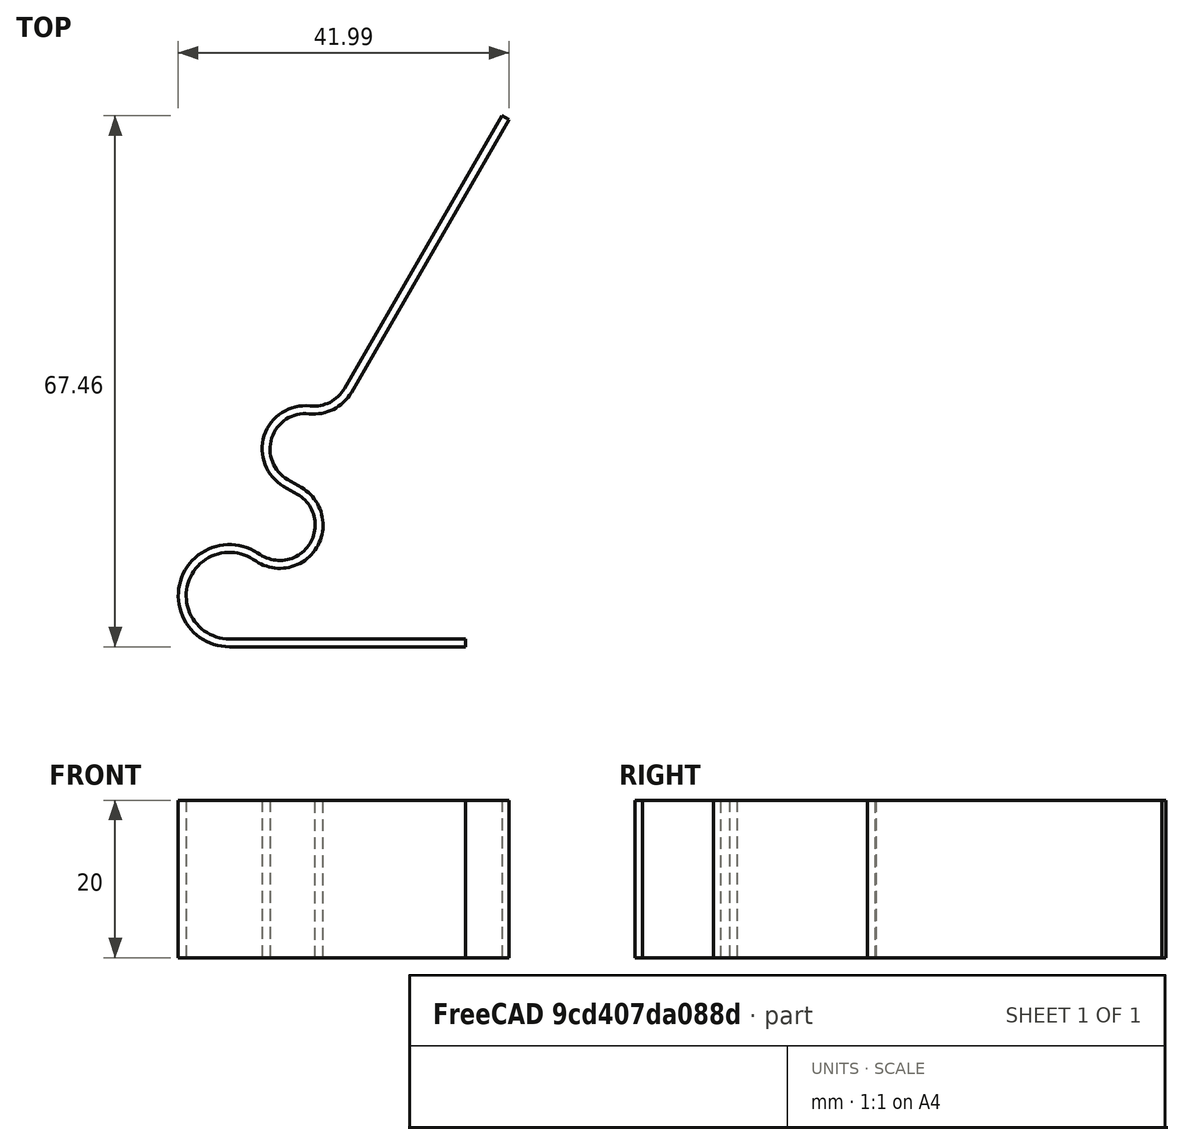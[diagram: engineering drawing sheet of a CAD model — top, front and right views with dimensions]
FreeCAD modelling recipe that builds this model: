
FCSTD DOCUMENT  (FreeCAD 2021.1015R24301 +3962 (Git))
Label: plastic_spring_catapult_1
License: All rights reserved
objects: Sketcher::SketchObject×2, Spreadsheet::Sheet×1, PartDesign::AdditivePipe×1, PartDesign::Body×1
note: 6 computed .brp shape members not serialized (recipe doc carries the construction recipe); baked Part::Feature solids carry a one-line shape summary decoded from their .brp

FEATURE [Spreadsheet::Sheet] Spreadsheet
  PythonMode = false
  cells = A1='height; B1(h)=20; A2='thickness; B2(thk)=1; A3='dia; B3(dia)=10; A4=center length; B4(l_center)=2; A5=center spacing; B5(cs)=10; C5=should be dia/2 really; A6=end length; B6(l_end)=40; A7=base length; B7(base_length)=30; A8=catapult angle; B8(a_catapult)=60; A9=bottom curve diameter; B9(dia_bot)=12
FEATURE [Sketcher::SketchObject] Sketch  label="profile"
  FullyConstrained = true
  MapMode = 5
  Placement = pos=(0,0,0) rot=(0.57735,0.57735,0.57735;2.0944rad)
  Support = -> [YZ_Plane]
  expr: Constraints[10] = Spreadsheet.thk / 2
  expr: Constraints[11] = Spreadsheet.thk
  expr: Constraints[9] = Spreadsheet.h
  sketch-geometry (4):
    g0: LineSegment StartX=-0.5 StartY=0 StartZ=0 EndX=0.5 EndY=0 EndZ=0
    g1: LineSegment StartX=0.5 StartY=0 StartZ=0 EndX=0.5 EndY=20 EndZ=0
    g2: LineSegment StartX=0.5 StartY=20 StartZ=0 EndX=-0.5 EndY=20 EndZ=0
    g3: LineSegment StartX=-0.5 StartY=20 StartZ=0 EndX=-0.5 EndY=0 EndZ=0
  constraints (12):
    c: Coincident(g0,g1)
    c: Coincident(g1,g2)
    c: Coincident(g2,g3)
    c: Coincident(g3,g0)
    c: Horizontal(g0)
    c: Horizontal(g2)
    c: Vertical(g1)
    c: Vertical(g3)
    c: PointOnObject(g0,g-1)
    c: DistanceY(g3,g3) = 20
    c: DistanceX(g0,g-1) = 0.5
    c: DistanceX(g0,g0) = 1
FEATURE [Sketcher::SketchObject] Sketch001  label="path"
  FullyConstrained = false
  MapMode = 5
  Support = -> [XY_Plane]
  expr: Constraints[13] = Spreadsheet.a_catapult
  expr: Constraints[15] = Spreadsheet.dia
  expr: Constraints[16] = Spreadsheet.dia
  expr: Constraints[22] = Spreadsheet.cs
  expr: Constraints[23] = Spreadsheet.dia_bot / 2 + Spreadsheet.dia / 2
  expr: Constraints[24] = Spreadsheet.l_center
  expr: Constraints[25] = Spreadsheet.dia
  expr: Constraints[3] = Spreadsheet.base_length
  expr: Constraints[5] = Spreadsheet.dia_bot
  expr: Constraints[9] = Spreadsheet.l_end
  sketch-geometry (11):
    g0: LineSegment StartX=0 StartY=0 StartZ=0 EndX=-30 EndY=0 EndZ=0
    g1: ArcOfCircle CenterX=-30 CenterY=6 CenterZ=0 NormalX=0 NormalY=0 NormalZ=1 AngleXU=0 Radius=6 StartAngle=0.989803 EndAngle=4.71239
    g2: LineSegment StartX=-26.7069 StartY=11.0155 StartZ=0 EndX=-26.3623 EndY=10.7893 EndZ=0
    g3: ArcOfCircle CenterX=-23.6181 CenterY=14.9689 CenterZ=0 NormalX=0 NormalY=0 NormalZ=1 AngleXU=0 Radius=5 StartAngle=4.1314 EndAngle=7.33038
    g4: LineSegment StartX=-21.1181 StartY=19.299 StartZ=0 EndX=-22.8501 EndY=20.299 EndZ=0
    g5: LineSegment StartX=-14.9476 StartY=32.0715 StartZ=0 EndX=5.05237 EndY=66.7125 EndZ=0
    g6: ArcOfCircle CenterX=-20.3501 CenterY=24.6291 CenterZ=0 NormalX=0 NormalY=0 NormalZ=1 AngleXU=0 Radius=5 StartAngle=1.46335 EndAngle=4.18879
    g7: ArcOfCircle CenterX=-19.2778 CenterY=34.5715 CenterZ=0 NormalX=0 NormalY=0 NormalZ=1 AngleXU=0 Radius=5 StartAngle=4.60495 EndAngle=5.75959
    g8: LineSegment [constr] StartX=-25.3501 StartY=15.9689 StartZ=0 EndX=-23.6181 EndY=14.9689 EndZ=0
    g9: LineSegment [constr] StartX=-25.3501 StartY=15.9689 StartZ=0 EndX=-20.3501 EndY=24.6291 EndZ=0
    g10: LineSegment [constr] StartX=-30 StartY=6 StartZ=0 EndX=5.05237 EndY=66.7125 EndZ=0
  constraints (34):
    c: Coincident(g0,g-1)
    c: PointOnObject(g0,g-1)
    c: Coincident(g1,g0)
    c: DistanceX(g0,g0) = 30
    c: Tangent(g1,g0)
    c: Diameter(g1) = 12
    c: Coincident(g2,g1)
    c: Coincident(g3,g2)
    c: Coincident(g4,g3)
    c: Distance(g5) = 40
    c: Tangent(g4,g3)
    c: Tangent(g2,g3)
    c: Tangent(g1,g2)
    c: Angle(g0,g5) = 1.0472
    c: Tangent(g6,g4)
    c: Diameter(g6) = 10
    c: Diameter(g3) = 10
    c: Coincident(g7,g6)
    c: Coincident(g7,g5)
    c: Tangent(g7,g5)
    c: Tangent(g6,g7)
    c: Coincident(g8,g3)
    c: Distance(g8,g6) = 10
    c: Distance(g1,g8) = 11
    c: Distance(g8) = 2
    c: Diameter(g7) = 10
    c: Coincident(g9,g8)
    c: Coincident(g9,g6)
    c: Coincident(g10,g1)
    c: Parallel(g10,g5)
    c: Coincident(g6,g4)
    c: Perpendicular(g8,g9)
    c: Coincident(g10,g5)
    c: Parallel(g9,g10)
FEATURE [PartDesign::AdditivePipe] AdditivePipe
  AuxilleryCurvelinear = true
  AuxillerySpineTangent = false
  Binormal = (0,0,0)
  ClaimChildren = false
  Fit = 0
  FitJoin = 0
  InnerFit = 0
  InnerFitJoin = 0
  Mode = 0
  NewSolid = false
  Placement = pos=(0,0,0) rot=(0.57735,0.57735,0.57735;2.0944rad)
  Profile = -> Sketch
  Spine = -> Sketch001
  SpineTangent = false
  Suppress = false
  Transformation = 0
  Transition = 1
  _ProfileBasedVersion = 1
FEATURE [PartDesign::Body] Body
  AutoGroupSolids = false
  ExportMode = 0
  Group = -> [Sketch,Sketch001,AdditivePipe]
  Origin = -> Origin
  Tip = -> AdditivePipe
  _ExportChildren = -> [AdditivePipe]
  _GroupVersion = 1
